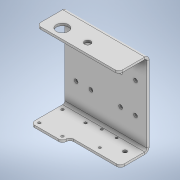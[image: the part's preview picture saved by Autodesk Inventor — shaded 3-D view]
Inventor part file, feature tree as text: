
AUTODESK INVENTOR PART (.ipt)
format: ipt  version: 2020 (Build 240168000, 168)  size: 274,944 bytes
history: native  units: in
note: dims shown in document units (in); Inventor stores cm internally (conversion verified against a paired STEP export)
features: sketch x9, hole x6, sheet_metal_op x3, chamfer x1, other x1
ambient origin geometry x8: Origin, YZ Plane, XZ Plane, XY Plane, X Axis, Y Axis, Z Axis, Center Point
bodies: Solid1 (feature_tree)
feature tree (20):
  sheet_metal_op  "Face1"
  sheet_metal_op  "Fold2"
  sheet_metal_op  "Fold3"
  hole  "Hole1"  [1 undecoded]
  hole  "Hole2"  [1 undecoded]
  chamfer  "Corner Round1"
  hole  "Hole4"  [1 undecoded]
  hole  "Hole5"  [1 undecoded]
  hole  "Hole6"  [1 undecoded]
  hole  "Hole7"  [1 undecoded]
  sketch  "Sketch2"  dims[d4=2.1654in d5=2.1654in]
  other  "Plate1"
  sketch  "Sketch4"  dims[d6=3.622in d7=7.5591in]
  sketch  "Sketch5"  dims[d8=0.1181in d17=2.126in]
  sketch  "Sketch6"  dims[d18=0.1181in d19=0.0591in]
  sketch  "Sketch7"  dims[d20=0.2362in d21=0.1181in]
  sketch  "Sketch9"  dims[d22=90.0deg d23=0.1181in d24=2.126in]
  sketch  "Sketch10"  dims[d25=0.1181in]
  sketch  "Sketch11"  dims[d26=0.0591in]
  sketch  "Sketch12"  dims[d27=0.2362in d28=0.1181in d29=90.0deg d30=0.1181in d31=0.8in d32=0.8in d33=0.2008in d35=0.7815in d37=0.2008in d38=0.2362in d39=0.1575in d40=0.0787in d41=90.0deg d42=0.1181in d43=0.8108in d44=0.7815in d45=0.2008in d46=0.2008in d47=1.5689in d48=1.5689in d49=0.2008in d50=0.2008in d51=0.2008in d52=0.2008in d53=0.7815in d54=1.5689in d55=1.5689in d56=0.7815in d57=0.2008in d61=0.3346in d62=0.0in d63=0.3228in d64=0.2362in d65=0.1575in d66=0.0787in d67=90.0deg d68=0.1181in d69=0.8108in d73=1.6654in d74=0.3937in d77=0.1969in d104=0.122in d105=0.122in d106=0.122in d107=1.1811in d108=1.5748in d109=0.2953in d110=1.1811in d111=1.378in d112=1.378in d113=0.122in d114=0.2362in d115=0.1575in d116=0.0787in d117=90.0deg d118=0.1181in d119=0.8108in d123=2.1654in d125=0.2008in d126=0.5413in d127=0.7874in d128=0.2008in d129=0.2362in d130=0.1575in d131=0.0787in d132=90.0deg d133=0.1181in d134=0.8108in d135=1.3327in d148=0.6378in d149=0.8327in d154=0.8327in d155=0.8327in d156=0.6378in d157=0.2362in d158=0.1575in d159=0.0787in d160=90.0deg d161=0.1181in d162=0.8108in d164=0.1654in d165=0.1654in d166=0.1654in d167=0.1654in d168=0.2224in d169=1.2205in d170=1.2205in d171=1.2205in d172=1.2205in d173=0.2224in d174=0.2224in d175=0.1378in d176=0.2362in d177=0.1575in d178=0.0787in d179=90.0deg d180=0.1181in d181=0.8108in d58=0.0394in d59=0.0394in d60=0.0394in d92=0.0394in d93=0.0394in d94=0.0394in d95=0.0059in d96=0.0098in d97=0.0148in d98=0.5635in d99=0.0295in d100=0.8108in d101=0.0025in d102=0.0295in d103=0.0148in d136=0.0148in]
note: 6 required parameter values undecoded (feature->parameter linkage not recoverable at this tier; creation-order binding heuristic only, values carry confidence <= 0.55)
